SOLIDWORKS PART (.sldprt)
format: sldprt  version: not decoded by parser v0  size: 83,456 bytes
history: native  units: mm
features: plane x5, sketch x4, extrude x2, material x1, fillet x1, sweep x1, mirror x1 (+9 scaffold rows collapsed)
feature tree (24):
  scaffold x9  (default folders/planes/origin — collapsed)
  material  "Matériau <non spécifié>"
  plane  "Face"
  plane  "Dessus"
  plane  "Droite"
  sketch  "Esquisse1"  dims[D1=2.5mm]
  extrude  "Base-Extrusion"  Depth=13.5mm
  sketch  "Esquisse2"  dims[D1=2.8mm]
  extrude  "Boss.-Extru.1"  Depth=1mm
  fillet  "Congé1"  Radius=5mm
  sketch  "Esquisse3"  dims[D2=~0.313663mm D1=1.27mm]
  plane  "Plan1"
  sketch  "Esquisse4"  dims[D1=17.0mm D2=4.0mm]
  sweep  "Balayage1"
  plane  "Plan2"  Offset=0mm
  mirror  "Symétrie1"
decode coverage: 7 of 9 modeling features carry decoded parameters
note: ~ marks probable driven/reference dimensions
note: suppression state not decoded; provenance and decode notes live in map.json
